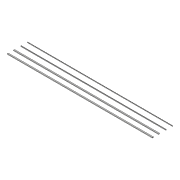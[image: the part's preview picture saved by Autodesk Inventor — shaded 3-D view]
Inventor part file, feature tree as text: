
AUTODESK INVENTOR PART (.ipt)
format: ipt  version: 2019.4 (Build 234330000, 330)  size: 98,304 bytes
history: native  units: mm
features: extrude x1, sketch x1
ambient origin geometry x8: Origin, YZ Plane, XZ Plane, XY Plane, X Axis, Y Axis, Z Axis, Center Point
bodies: Solid1 (feature_tree)
feature tree (2):
  extrude  "Extrusion1"  Depth=0.5mm
  sketch  "Sketch1"  dims[d0=70.0mm d1=0.5mm d2=70.0mm d3=0.2mm d4=3.0mm d5=70.0mm d6=0.1mm d7=3.0mm d8=0.0mm d9=70.0mm d10=0.5mm d11=3.0mm d12=0.0mm d13=0.3mm d14=0.0mm]
